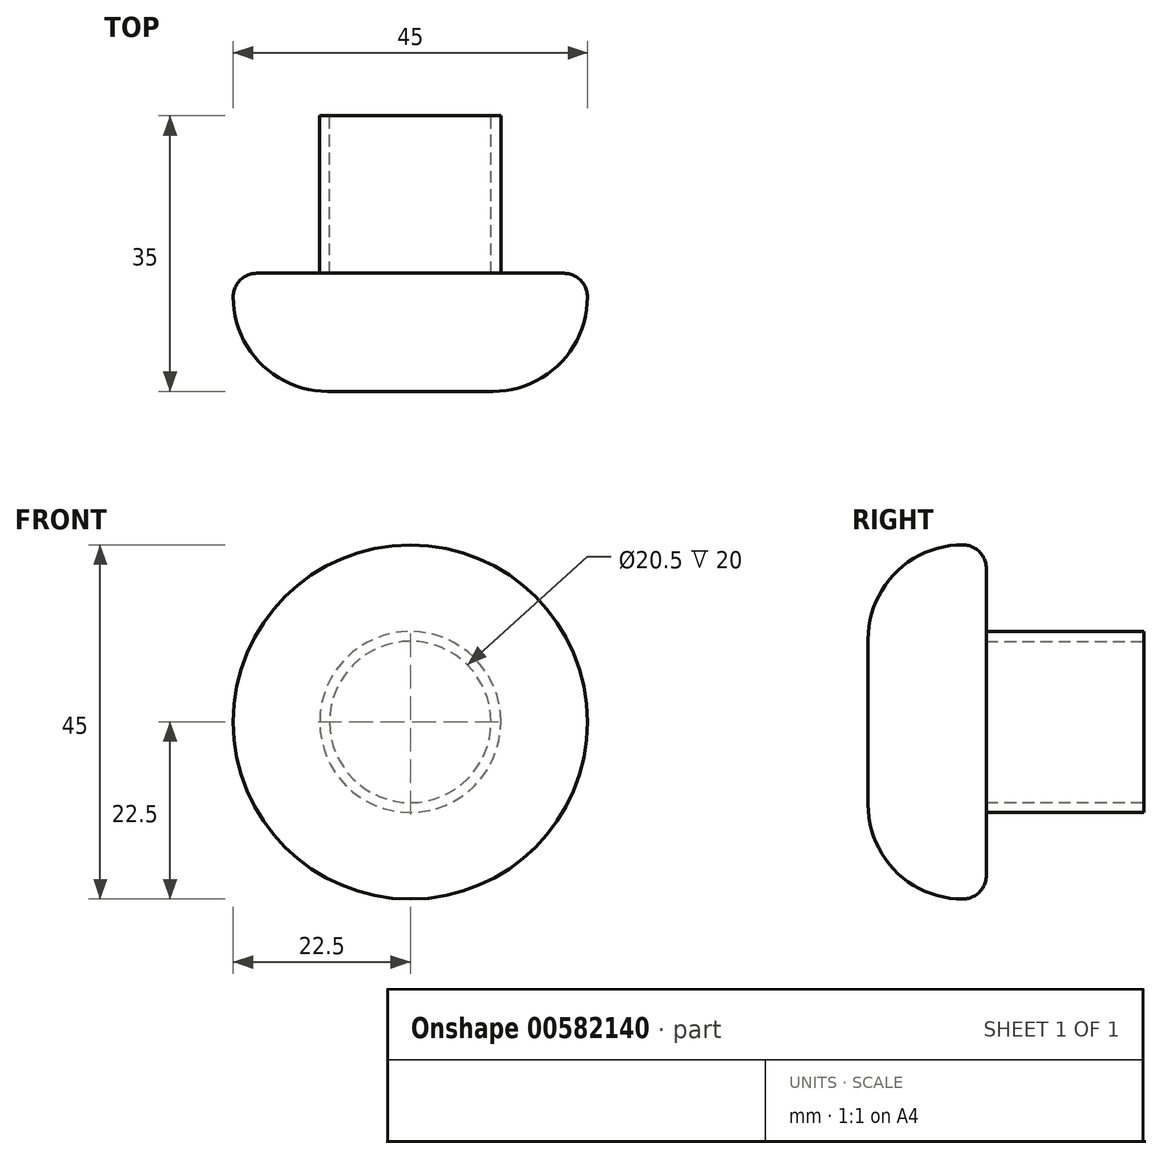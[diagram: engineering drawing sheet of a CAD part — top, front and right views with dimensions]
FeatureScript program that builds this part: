
annotation { "Feature Type Name" : "Feature", "Feature Type Description" : "" }
export const myFeature = defineFeature(function(context is Context, id is Id, definition is map)
    precondition{}
    {
        {
            var Q0;
            Q0=qCreatedBy(makeId("Front.planeOp"),FACE);
            var sketch = newSketch(context, id + "F0", { "sketchPlane" : qUnion([Q0])});
            skCircle(sketch, "E0", {"center": v(0, 0) * mm, "radius": 10.25 * mm});
            skCircle(sketch, "E1", {"center": v(0, 0) * mm, "radius": 11.5 * mm});
            skSolve(sketch);
        }
        {
            var Q0;
            Q0 = qSketchRegion(id + "F0", true);
            extrude(context, id + "F1", {"entities" : qUnion([Q0]), "depth" : 20 * mm, "offsetDistance" : 25 * mm});
        }
        {
            var Q0;
            Q0=makeQuery(id+"F1.opExtrude","CAP_FACE",FACE,{"disambiguationData":[OSD([sQuery(id+"F0.wireOp",EDGE,"E0"),sQuery(id+"F0.wireOp",EDGE,"E1")])],"isStart":false});
            var sketch = newSketch(context, id + "F2", { "sketchPlane" : qUnion([Q0])});
            skCircle(sketch, "E2", {"center": v(0, 0) * mm, "radius": 22.5 * mm});
            skSolve(sketch);
        }
        {
            var Q0;
            Q0 = qSketchRegion(id + "F2", true);
            extrude(context, id + "F3", {"entities" : qUnion([Q0]), "operationType" : NewBodyOperationType.ADD, "depth" : 15 * mm, "offsetDistance" : 25 * mm});
        }
        {
            var Q0;
            Q0=makeQuery(id+"F3.opExtrude","CAP_FACE",FACE,{"disambiguationData":[OSD([sQuery(id+"F2.wireOp",EDGE,"E2")])],"isStart":false});
            fillet(context, id + "F4", {"entities" : qUnion([Q0]), "radius" : 12 * mm, "tangentPropagation" : true, "allowEdgeOverflow" : false});
        }
        {
            var Q0;
            {var subQ0=sQuery(id+"F2.wireOp",EDGE,"E2");Q0=makeQuery(id+"F4.opFillet","BLEND_EDGE",EDGE,{"blendedFrom":[makeQuery(id+"F3.opExtrude","CAP_EDGE",EDGE,{"disambiguationData":[OSD([subQ0])],"isStart":false}),makeQuery(id+"F3.opExtrude","CAP_FACE",FACE,{"disambiguationData":[OSD([subQ0])],"isStart":false})],"blendedInto":[makeQuery(id+"F3.opExtrude","CAP_FACE",FACE,{"disambiguationData":[OSD([subQ0])],"isStart":false})]});}
            var Q1;
            {var subQ0=sQuery(id+"F2.wireOp",EDGE,"E2");Q1=makeQuery(id+"F4.opFillet","BLEND_EDGE",EDGE,{"blendedFrom":[makeQuery(id+"F3.opExtrude","CAP_EDGE",EDGE,{"disambiguationData":[OSD([subQ0])],"isStart":false}),makeQuery(id+"F3.opExtrude","SWEPT_FACE",FACE,{"disambiguationData":[OSD([subQ0])]})],"blendedInto":[makeQuery(id+"F3.opExtrude","SWEPT_FACE",FACE,{"disambiguationData":[OSD([subQ0])]})]});}
            var Q2;
            Q2=makeQuery(id+"F3.opExtrude","CAP_EDGE",EDGE,{"disambiguationData":[OSD([sQuery(id+"F2.wireOp",EDGE,"E2")])],"isStart":true});
            fillet(context, id + "F5", {"entities" : qUnion([Q0, Q1, Q2]), "radius" : 3 * mm, "tangentPropagation" : true, "allowEdgeOverflow" : false});
        }
    });
